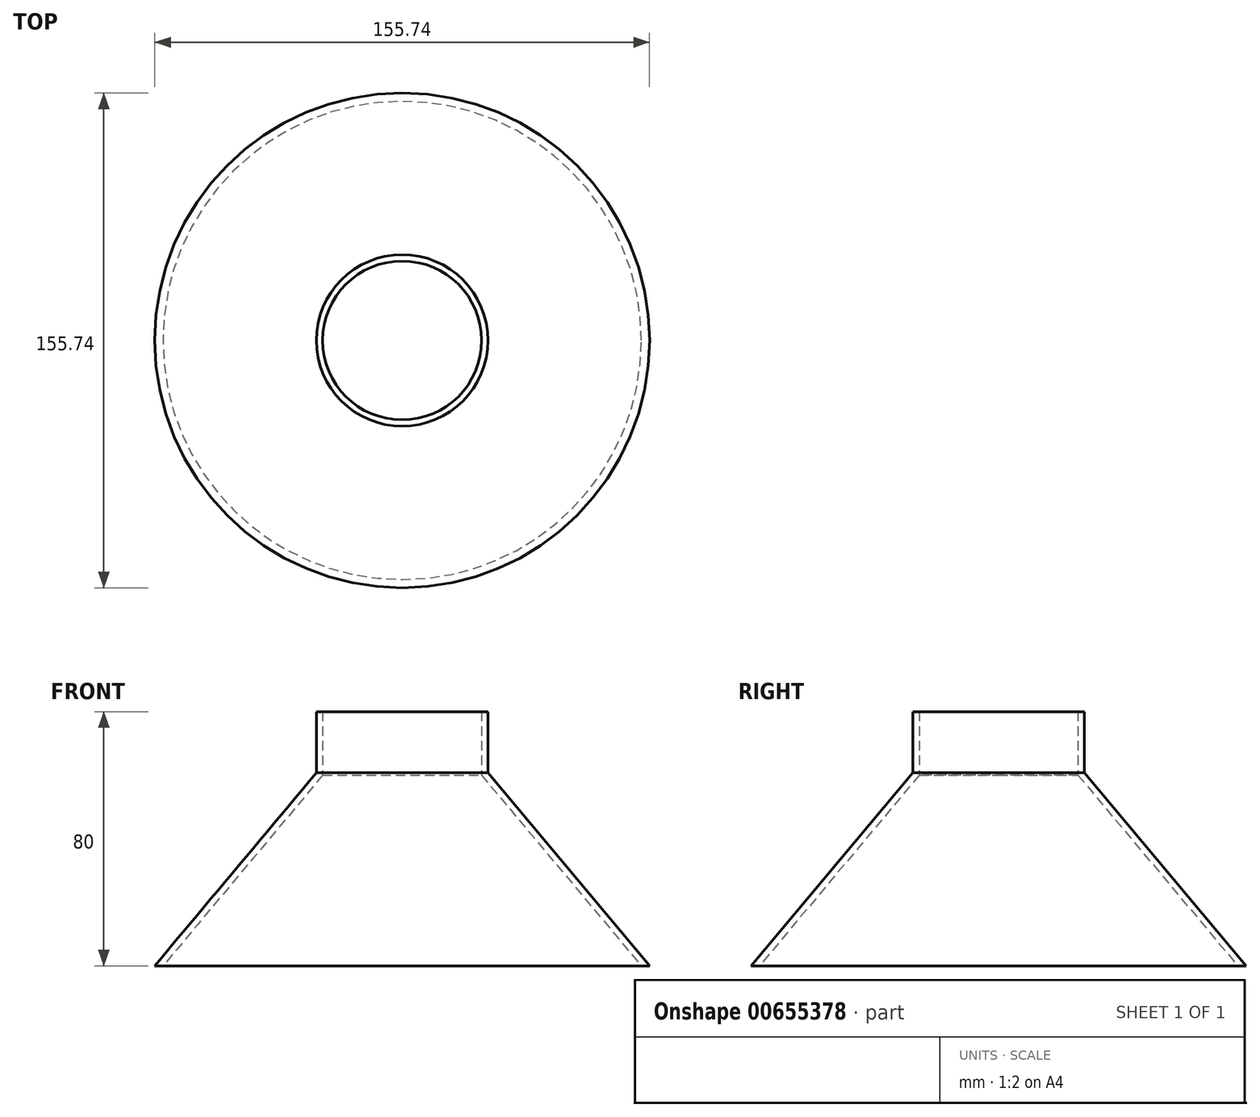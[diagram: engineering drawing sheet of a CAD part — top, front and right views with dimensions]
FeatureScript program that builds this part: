
annotation { "Feature Type Name" : "Feature", "Feature Type Description" : "" }
export const myFeature = defineFeature(function(context is Context, id is Id, definition is map)
    precondition{}
    {
        {
            var Q0;
            Q0=qCreatedBy(makeId("Front.planeOp"),FACE);
            var sketch = newSketch(context, id + "F0", { "sketchPlane" : qUnion([Q0])});
            skLineSegment(sketch, "E0", {"start": v(0, 0) * mm, "end": v(0, 80) * mm, "construction": true});
            skLineSegment(sketch, "E1", {"start": v(0, 80) * mm, "end": v(25, 80) * mm, "construction": true});
            skLineSegment(sketch, "E2", {"start": v(25, 80) * mm, "end": v(25, 60) * mm});
            skLineSegment(sketch, "E3", {"start": v(25, 60) * mm, "end": v(75.27, 0) * mm});
            skLineSegment(sketch, "E4.0", {"start": v(27, 60.73) * mm, "end": v(77.87, 0) * mm});
            skLineSegment(sketch, "E4.1", {"start": v(27, 80) * mm, "end": v(27, 60.73) * mm});
            skLineSegment(sketch, "E5", {"start": v(25, 80) * mm, "end": v(27, 80) * mm});
            skLineSegment(sketch, "E6", {"start": v(75.27, 0) * mm, "end": v(77.87, 0) * mm});
            skSolve(sketch);
        }
        {
            var Q0;
            Q0=makeQuery(id+"F0.imprint","IMPRINT",FACE,{"disambiguationData":[TD([[makeQuery(id+"F0.imprint","IMPRINT",EDGE,{"derivedFrom":sQuery(id+"F0.wireOp",EDGE,"E2")}),1.0]])]});
            var Q1;
            Q1=sQuery(id+"F0.wireOp",EDGE,"E0");
            revolve(context, id + "F1", {"surfaceOperationType" : NewSurfaceOperationType.NEW, "entities" : qUnion([Q0]), "axis" : qUnion([Q1]), "revolveType" : RevolveType.FULL});
        }
    });
